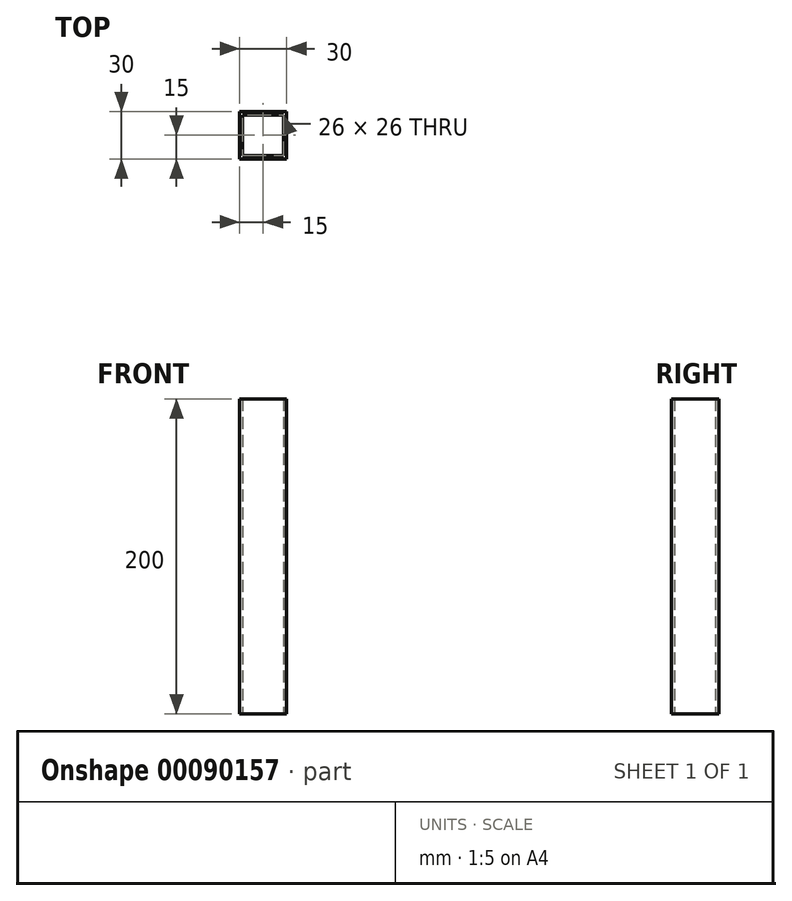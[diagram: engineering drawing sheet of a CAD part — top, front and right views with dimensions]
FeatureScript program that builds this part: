
annotation { "Feature Type Name" : "Feature", "Feature Type Description" : "" }
export const myFeature = defineFeature(function(context is Context, id is Id, definition is map)
    precondition{}
    {
        {
            var Q0;
            Q0=qCreatedBy(makeId("Top.planeOp"),FACE);
            var sketch = newSketch(context, id + "F0", { "sketchPlane" : qUnion([Q0])});
            skPoint(sketch, "E0.middle", {"position": v(0, 0) * mm});
            skLineSegment(sketch, "E1.bottom", {"start": v(15, -15) * mm, "end": v(-15, -15) * mm});
            skLineSegment(sketch, "E1.top", {"start": v(15, 15) * mm, "end": v(-15, 15) * mm});
            skLineSegment(sketch, "E1.left", {"start": v(15, -15) * mm, "end": v(15, 15) * mm});
            skLineSegment(sketch, "E1.right", {"start": v(-15, -15) * mm, "end": v(-15, 15) * mm});
            skLineSegment(sketch, "E2.bottom", {"start": v(13, -13) * mm, "end": v(-13, -13) * mm});
            skLineSegment(sketch, "E2.top", {"start": v(13, 13) * mm, "end": v(-13, 13) * mm});
            skLineSegment(sketch, "E2.left", {"start": v(13, -13) * mm, "end": v(13, 13) * mm});
            skLineSegment(sketch, "E2.right", {"start": v(-13, -13) * mm, "end": v(-13, 13) * mm});
            skSolve(sketch);
        }
        {
            var Q0;
            Q0=qSketchRegion(id+"F0",true);
            extrude(context, id + "F1", {"entities" : qUnion([Q0]), "depth" : 200 * mm});
        }
    });
